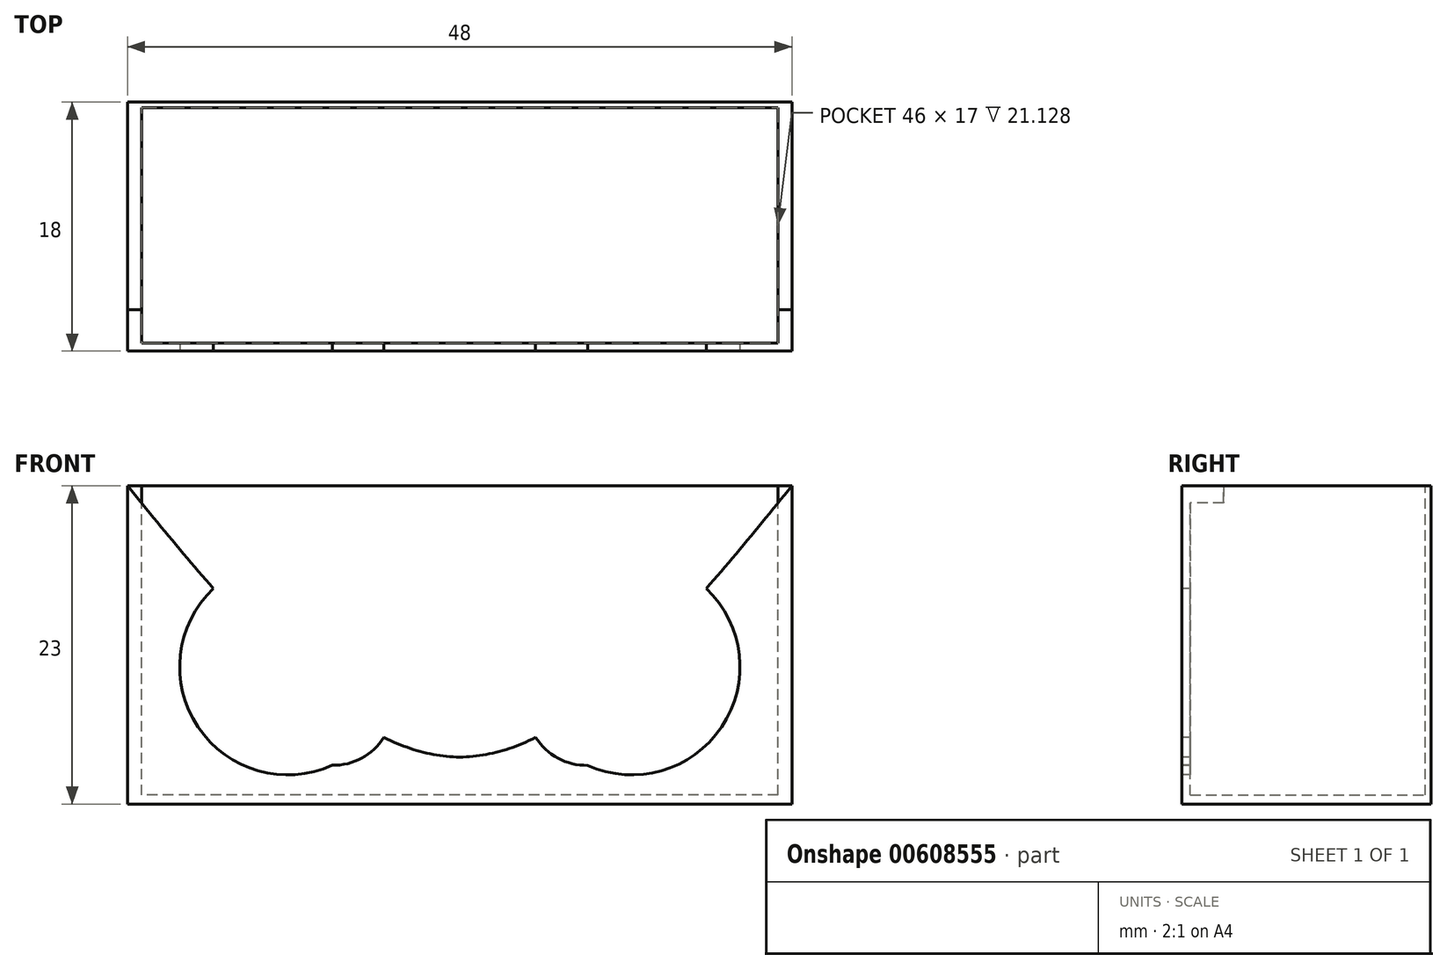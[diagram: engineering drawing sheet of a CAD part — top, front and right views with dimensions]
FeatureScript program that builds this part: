
annotation { "Feature Type Name" : "Feature", "Feature Type Description" : "" }
export const myFeature = defineFeature(function(context is Context, id is Id, definition is map)
    precondition{}
    {
        {
            var Q0;
            Q0=qCreatedBy(makeId("Front.planeOp"),FACE);
            var sketch = newSketch(context, id + "F0", { "sketchPlane" : qUnion([Q0])});
            skLineSegment(sketch, "E0.bottom", {"start": v(24, -11.5) * mm, "end": v(-24, -11.5) * mm});
            skLineSegment(sketch, "E0.top", {"start": v(24, 11.5) * mm, "end": v(-24, 11.5) * mm});
            skLineSegment(sketch, "E0.left", {"start": v(24, -11.5) * mm, "end": v(24, 11.5) * mm});
            skLineSegment(sketch, "E0.right", {"start": v(-24, -11.5) * mm, "end": v(-24, 11.5) * mm});
            skPoint(sketch, "E0.middle", {"position": v(0, 0) * mm});
            skSolve(sketch);
        }
        {
            var Q0;
            Q0 = qSketchRegion(id + "F0", true);
            extrude(context, id + "F1", {"entities" : qUnion([Q0]), "depth" : 18 * mm, "offsetDistance" : 25.4 * mm});
        }
        {
            var Q0;
            Q0=makeQuery(id+"F1.opExtrude","SWEPT_FACE",FACE,{"disambiguationData":[OSD([sQuery(id+"F0.wireOp",EDGE,"E0.top")])]});
            var sketch = newSketch(context, id + "F2", { "sketchPlane" : qUnion([Q0])});
            skLineSegment(sketch, "E1.bottom", {"start": v(23, -17.4) * mm, "end": v(-23, -17.4) * mm});
            skLineSegment(sketch, "E1.top", {"start": v(23, -0.4) * mm, "end": v(-23, -0.4) * mm});
            skLineSegment(sketch, "E1.left", {"start": v(23, -17.4) * mm, "end": v(23, -0.4) * mm});
            skLineSegment(sketch, "E1.right", {"start": v(-23, -17.4) * mm, "end": v(-23, -0.4) * mm});
            skPoint(sketch, "E1.middle", {"position": v(0, -8.9) * mm});
            skSolve(sketch);
        }
        {
            var Q0;
            Q0 = qSketchRegion(id + "F2", true);
            extrude(context, id + "F3", {"entities" : qUnion([Q0]), "operationType" : NewBodyOperationType.REMOVE, "oppositeDirection" : true, "depth" : 22.35 * mm, "offsetDistance" : 25.4 * mm});
        }
        {
            var Q0;
            Q0=makeQuery(id+"F1.opExtrude","CAP_FACE",FACE,{"disambiguationData":[OSD([sQuery(id+"F0.wireOp",EDGE,"E0.bottom"),sQuery(id+"F0.wireOp",EDGE,"E0.top"),sQuery(id+"F0.wireOp",EDGE,"E0.left"),sQuery(id+"F0.wireOp",EDGE,"E0.right")])],"isStart":false});
            var sketch = newSketch(context, id + "F4", { "sketchPlane" : qUnion([Q0])});
            skLineSegment(sketch, "E2", {"start": v(0, -11.5) * mm, "end": v(0, 0) * mm});
            skFitSpline(sketch, "E3", {"points": [v(-24, 11.5) * mm, v(0, -8.1) * mm, v(24, 11.5) * mm], "startDerivative": vector(48, -58.8) * mm, "endDerivative": vector(48, 58.8) * mm});
            skLineSegment(sketch, "E4", {"start": v(-24, 11.5) * mm, "end": v(24, 11.5) * mm});
            skArc(sketch, "E5", {"start": v(-12.43, -1.58) * mm, "mid": v(-7.69, -8.45) * mm, "end": v(-8.36, -0.13) * mm});
            skArc(sketch, "E6", {"start": v(8.36, -0.13) * mm, "mid": v(7.69, -8.45) * mm, "end": v(12.43, -1.58) * mm});
            skFitSpline(sketch, "E7.trimOffspring", {"points": [v(-24, 11.5) * mm, v(0, -8.1) * mm, v(24, 11.5) * mm], "startDerivative": vector(48, -58.8) * mm, "endDerivative": vector(48, 58.8) * mm});
            skFitSpline(sketch, "E8.trimOffspring", {"points": [v(-24, 11.5) * mm, v(0, -8.1) * mm, v(24, 11.5) * mm], "startDerivative": vector(48, -58.8) * mm, "endDerivative": vector(48, 58.8) * mm});
            skCircle(sketch, "E9", {"center": v(-12.43, -1.58) * mm, "radius": 7.81 * mm});
            skCircle(sketch, "E10", {"center": v(12.43, -1.58) * mm, "radius": 7.81 * mm});
            skSolve(sketch);
        }
        {
            var Q0;
            Q0 = qSketchRegion(id + "F4", true);
            extrude(context, id + "F5", {"entities" : qUnion([Q0]), "operationType" : NewBodyOperationType.REMOVE, "oppositeDirection" : true, "depth" : 3 * mm, "offsetDistance" : 25.4 * mm});
        }
    });
